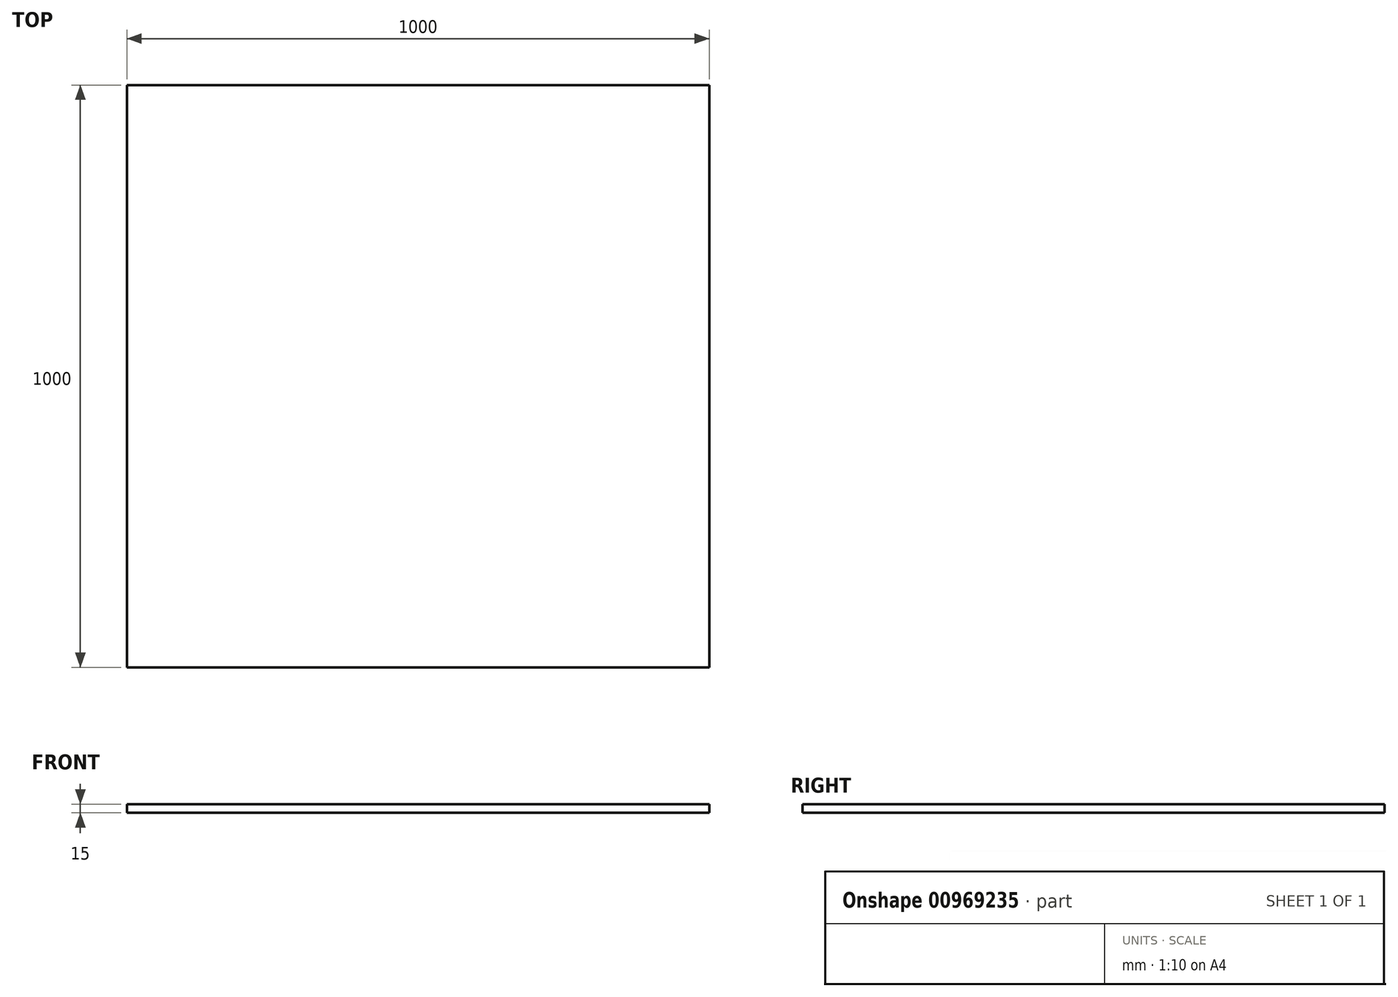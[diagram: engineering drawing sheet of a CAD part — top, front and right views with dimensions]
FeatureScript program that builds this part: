
annotation { "Feature Type Name" : "Feature", "Feature Type Description" : "" }
export const myFeature = defineFeature(function(context is Context, id is Id, definition is map)
    precondition{}
    {
        {
            var Q0;
            Q0=qCreatedBy(makeId("Top.planeOp"),FACE);
            var sketch = newSketch(context, id + "F0", { "sketchPlane" : qUnion([Q0])});
            skLineSegment(sketch, "E0.bottom", {"start": v(500, 500) * mm, "end": v(-500, 500) * mm});
            skLineSegment(sketch, "E0.top", {"start": v(500, -500) * mm, "end": v(-500, -500) * mm});
            skLineSegment(sketch, "E0.left", {"start": v(500, 500) * mm, "end": v(500, -500) * mm});
            skLineSegment(sketch, "E0.right", {"start": v(-500, 500) * mm, "end": v(-500, -500) * mm});
            skPoint(sketch, "E0.middle", {"position": v(0, 0) * mm});
            skSolve(sketch);
        }
        {
            var Q0;
            Q0=makeQuery(id+"F0.imprint","IMPRINT",FACE,{"disambiguationData":[TD([[makeQuery(id+"F0.imprint","IMPRINT",EDGE,{"derivedFrom":sQuery(id+"F0.wireOp",EDGE,"E0.bottom")}),1.0]])]});
            extrude(context, id + "F1", {"entities" : qUnion([Q0]), "depth" : 15 * mm, "offsetDistance" : 25 * mm});
        }
    });
